# Revit family: Bath-Drain-KOHLER-K-19321T
name_source: partatom
category: Plumbing Fixtures
revit_build: Autodesk Revit 2017 (Build: 20160225_1515(x64)
units: mm (PartAtom-declared; Revit-internal decimal feet)

## family parameters
Cut with Voids When Loaded = No
Host = Face
OmniClass Number = 23.31.15.17.23
OmniClass Title = Bathtub Drains
Part Type = Normal
Room Calculation Point = No
Round Connector Dimension = Use Diameter
Shared = No

## types (3) — shared parameters
ADA Compliant = No
Assembly Code = D2010500
CW Connection = No
Cold Water Inlet = Cold Water Inlet
Date Modified = 03/23/2021
Default Elevation = 0"
Description = Bathtub drain (copper pipe, white)
HW Connection = No
Height = 21 9/16"
Hot Water Inlet = Hot Water Inlet
Length = 3 3/8"
Manufacturer = KOHLER Co.
Master Format 2014 = 22 41 19
Master Format 2014 Name = Sanitary Drain
Material = Premium Metal Construction
Product Documentation Link = https://files.kohler.com.cn
Product Page URL = https://www.kohler.com.cn
URL = http://www.kohler.com.cn
Vent Connection = No
Waste Connection = Yes
Waste Water Outlet = Waste Water Outlet
WaterSense Certified = No
Width = 11 3/8"

## per-type parameters (varying)
| type | Finish | Model | Type |
| 0-White | Kohler-Metal-0-White | K-19321T-0 | 1 |
| CP-Polished Chrome | Kohler-Metal-CP-Polished_Chrome | K-19321T-CP | 2 |
| AF-Flange Gold | Kohler-Metal-AF-Flange_Gold | K-19321T-AF | 3 |

## geometry (parser evidence)
native form markers: Sweep x4
no freeform markers — native parametric forms only
